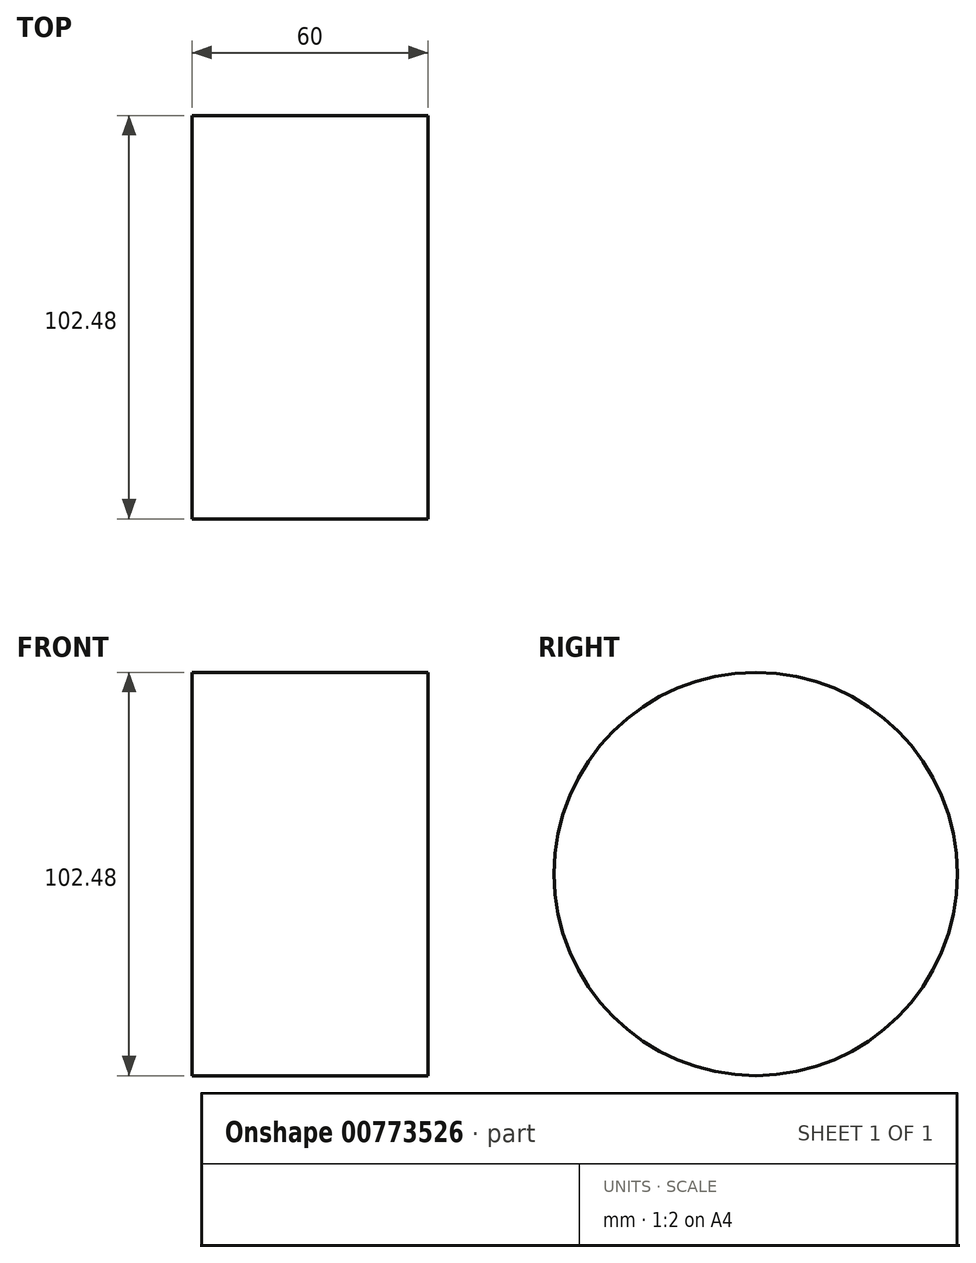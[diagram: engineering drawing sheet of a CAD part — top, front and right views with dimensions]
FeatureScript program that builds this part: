
annotation { "Feature Type Name" : "Feature", "Feature Type Description" : "" }
export const myFeature = defineFeature(function(context is Context, id is Id, definition is map)
    precondition{}
    {
        {
            var Q0;
            Q0=qCreatedBy(makeId("Right.planeOp"),FACE);
            var sketch = newSketch(context, id + "F0", { "sketchPlane" : qUnion([Q0])});
            skCircle(sketch, "E0", {"center": v(0, 0) * mm, "radius": 51.24 * mm});
            skSolve(sketch);
        }
        {
            var Q0;
            Q0 = qSketchRegion(id + "F0", true);
            extrude(context, id + "F1", {"entities" : qUnion([Q0]), "endBound" : BoundingType.SYMMETRIC, "depth" : 60 * mm, "offsetDistance" : 25 * mm});
        }
    });
